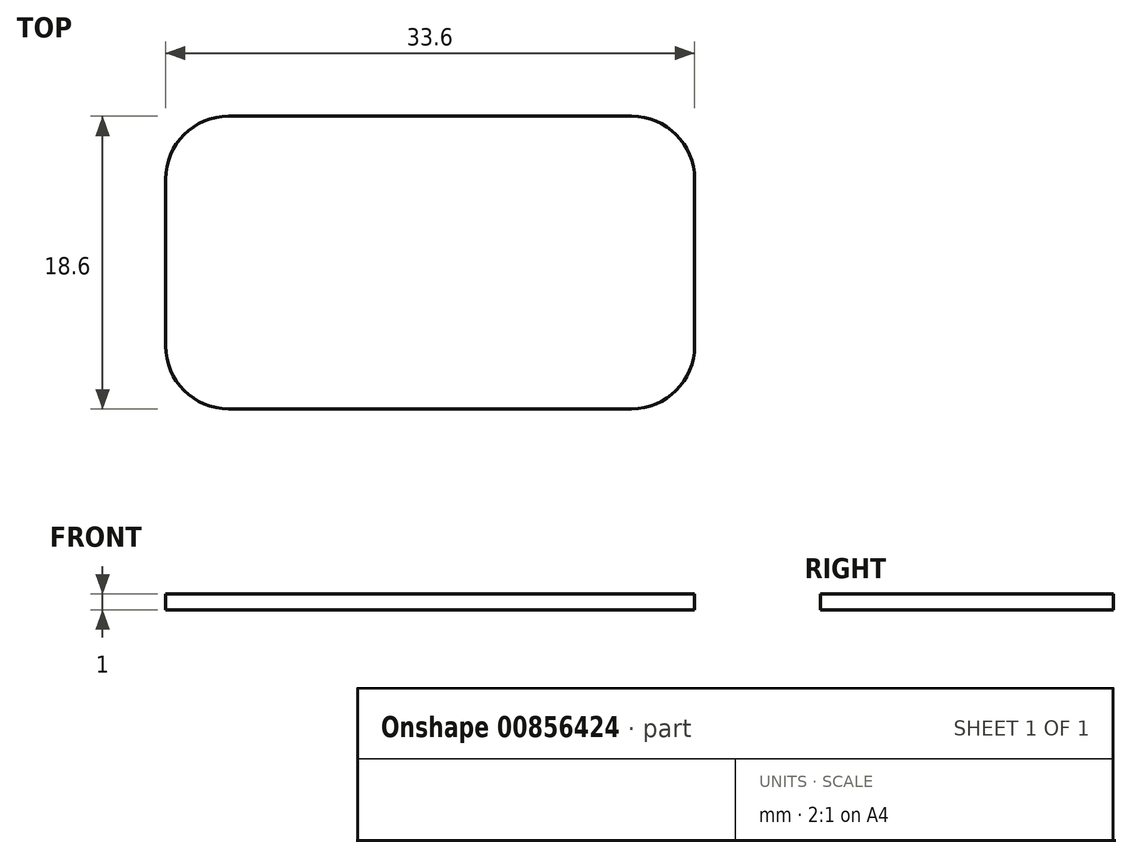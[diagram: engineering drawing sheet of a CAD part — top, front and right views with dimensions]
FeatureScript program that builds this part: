
annotation { "Feature Type Name" : "Feature", "Feature Type Description" : "" }
export const myFeature = defineFeature(function(context is Context, id is Id, definition is map)
    precondition{}
    {
        {
            var Q0;
            Q0=qCreatedBy(makeId("Top.planeOp"),FACE);
            var sketch = newSketch(context, id + "F0", { "sketchPlane" : qUnion([Q0])});
            skLineSegment(sketch, "E0.bottom", {"start": v(12.8, -8.5) * mm, "end": v(-12.8, -8.5) * mm});
            skLineSegment(sketch, "E0.top", {"start": v(12.8, 8.5) * mm, "end": v(-12.8, 8.5) * mm});
            skLineSegment(sketch, "E0.left", {"start": v(16, -5.3) * mm, "end": v(16, 5.3) * mm});
            skLineSegment(sketch, "E0.right", {"start": v(-16, -5.3) * mm, "end": v(-16, 5.3) * mm});
            skPoint(sketch, "E0.middle", {"position": v(0, 0) * mm});
            skPoint(sketch, "E1.visualSharp", {"position": v(-16, 8.5) * mm});
            skArc(sketch, "E1.filletArc", {"start": v(-12.8, 8.5) * mm, "mid": v(-15.06, 7.56) * mm, "end": v(-16, 5.3) * mm});
            skPoint(sketch, "E2.visualSharp", {"position": v(16, 8.5) * mm});
            skArc(sketch, "E2.filletArc", {"start": v(16, 5.3) * mm, "mid": v(15.06, 7.56) * mm, "end": v(12.8, 8.5) * mm});
            skPoint(sketch, "E3.visualSharp", {"position": v(16, -8.5) * mm});
            skArc(sketch, "E3.filletArc", {"start": v(12.8, -8.5) * mm, "mid": v(15.06, -7.56) * mm, "end": v(16, -5.3) * mm});
            skPoint(sketch, "E4.visualSharp", {"position": v(-16, -8.5) * mm});
            skArc(sketch, "E4.filletArc", {"start": v(-16, -5.3) * mm, "mid": v(-15.06, -7.56) * mm, "end": v(-12.8, -8.5) * mm});
            skArc(sketch, "E5.0", {"start": v(-16.8, -5.3) * mm, "mid": v(-15.63, -8.13) * mm, "end": v(-12.8, -9.3) * mm});
            skLineSegment(sketch, "E5.1", {"start": v(12.8, -9.3) * mm, "end": v(-12.8, -9.3) * mm});
            skLineSegment(sketch, "E5.2", {"start": v(-16.8, -5.3) * mm, "end": v(-16.8, 5.3) * mm});
            skArc(sketch, "E5.3", {"start": v(12.8, -9.3) * mm, "mid": v(15.63, -8.13) * mm, "end": v(16.8, -5.3) * mm});
            skArc(sketch, "E5.4", {"start": v(-12.8, 9.3) * mm, "mid": v(-15.63, 8.13) * mm, "end": v(-16.8, 5.3) * mm});
            skLineSegment(sketch, "E5.5", {"start": v(12.8, 9.3) * mm, "end": v(-12.8, 9.3) * mm});
            skArc(sketch, "E5.6", {"start": v(16.8, 5.3) * mm, "mid": v(15.63, 8.13) * mm, "end": v(12.8, 9.3) * mm});
            skLineSegment(sketch, "E5.7", {"start": v(16.8, -5.3) * mm, "end": v(16.8, 5.3) * mm});
            skSolve(sketch);
        }
        {
            var Q0;
            Q0=makeQuery(id+"F0.imprint","IMPRINT",FACE,{"disambiguationData":[TD([[makeQuery(id+"F0.imprint","IMPRINT",EDGE,{"derivedFrom":sQuery(id+"F0.wireOp",EDGE,"E0.bottom")}),1.0]])]});
            var Q1;
            Q1=makeQuery(id+"F0.imprint","IMPRINT",FACE,{"disambiguationData":[TD([[makeQuery(id+"F0.imprint","IMPRINT",EDGE,{"derivedFrom":sQuery(id+"F0.wireOp",EDGE,"E0.bottom")}),-1.0]])]});
            extrude(context, id + "F1", {"entities" : qUnion([Q0, Q1]), "depth" : 1 * mm, "offsetDistance" : 25 * mm});
        }
    });
